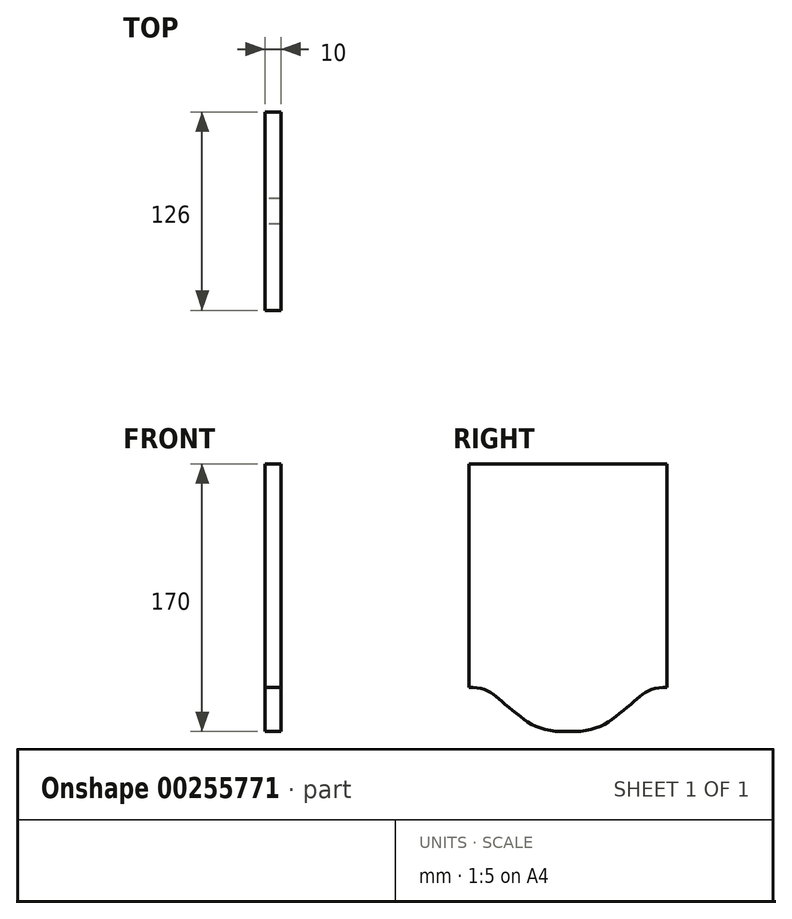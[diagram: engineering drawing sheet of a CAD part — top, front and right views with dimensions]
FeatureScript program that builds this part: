
annotation { "Feature Type Name" : "Feature", "Feature Type Description" : "" }
export const myFeature = defineFeature(function(context is Context, id is Id, definition is map)
    precondition{}
    {
        {
            var Q0;
            Q0=qCreatedBy(makeId("Right.planeOp"),FACE);
            var sketch = newSketch(context, id + "F0", { "sketchPlane" : qUnion([Q0])});
            skLineSegment(sketch, "E0.bottom", {"start": v(0, 0) * mm, "end": v(-126, 0) * mm});
            skLineSegment(sketch, "E0.top", {"start": v(0, 170) * mm, "end": v(-126, 170) * mm});
            skLineSegment(sketch, "E0.left", {"start": v(0, 0) * mm, "end": v(0, 170) * mm});
            skLineSegment(sketch, "E0.right", {"start": v(-126, 0) * mm, "end": v(-126, 170) * mm});
            skFitSpline(sketch, "E1", {"points": [v(0, 28) * mm, v(-9, 27) * mm, v(-15, 24) * mm, v(-21, 19) * mm, v(-31, 11) * mm, v(-41, 4) * mm, v(-55, 0) * mm], "startDerivative": vector(-60.92, -2.6) * mm, "endDerivative": vector(-75.26, -15.55) * mm});
            skFitSpline(sketch, "E2", {"points": [v(-126, 28) * mm, v(-117, 27) * mm, v(-111, 24) * mm, v(-105, 19) * mm, v(-95, 11) * mm, v(-85, 4) * mm, v(-71, 0) * mm], "startDerivative": vector(60.92, -2.6) * mm, "endDerivative": vector(75.26, -15.55) * mm});
            skSolve(sketch);
        }
        {
            var Q0;
            {var subQ1=sQuery(id+"F0.wireOp",EDGE,"E0.top");Q0=makeQuery(id+"F0.imprint","IMPRINT",FACE,{"disambiguationData":[TD([[makeQuery(id+"F0.imprint","IMPRINT",EDGE,{"derivedFrom":subQ1}),1.0]])]});}
            extrude(context, id + "F1", {"entities" : qUnion([Q0]), "depth" : 10 * mm});
        }
    });
